# Revit family: FU_Chair_Sandler_Kori 2-2LB
name_source: partatom
category: Furniture
units: mm (PartAtom-declared; Revit-internal decimal feet)

## family parameters
Always vertical = Yes
Cut with Voids When Loaded = No
OmniClass Number = 23.40.20.00
OmniClass Title = General Furniture and Specialties
Room Calculation Point = No
Shared = No
Work Plane-Based = No

## types (1)
- Kori 2.2LB
    Default Elevation = 0 mm  [stored 0 ft]
    Depth = 690 mm  [stored 2.26378 ft]
    Description = Swivel armchair with low backrest and 5 spoke cast aluminum alloy base fitted with gas lift column and 7 position tilt mechanism. SOFT TREAD casters for hard surface flooring is standard.
    Height = 830 mm  [stored 2.7231 ft]
    Manufacturer = Sandler
    Model = Kori 1.2LB
    Seat Material = Fabric - Gravity - Frozen CPC27
    URL = https://www.sandlerseating.com
    Width = 740 mm  [stored 2.42782 ft]

note: [stored X ft] marks values corroborated as IEEE doubles in the binary element streams (Revit-internal decimal feet)

## geometry (parser evidence)
native form markers: Blend x2, Sweep x13
no freeform markers — native parametric forms only
